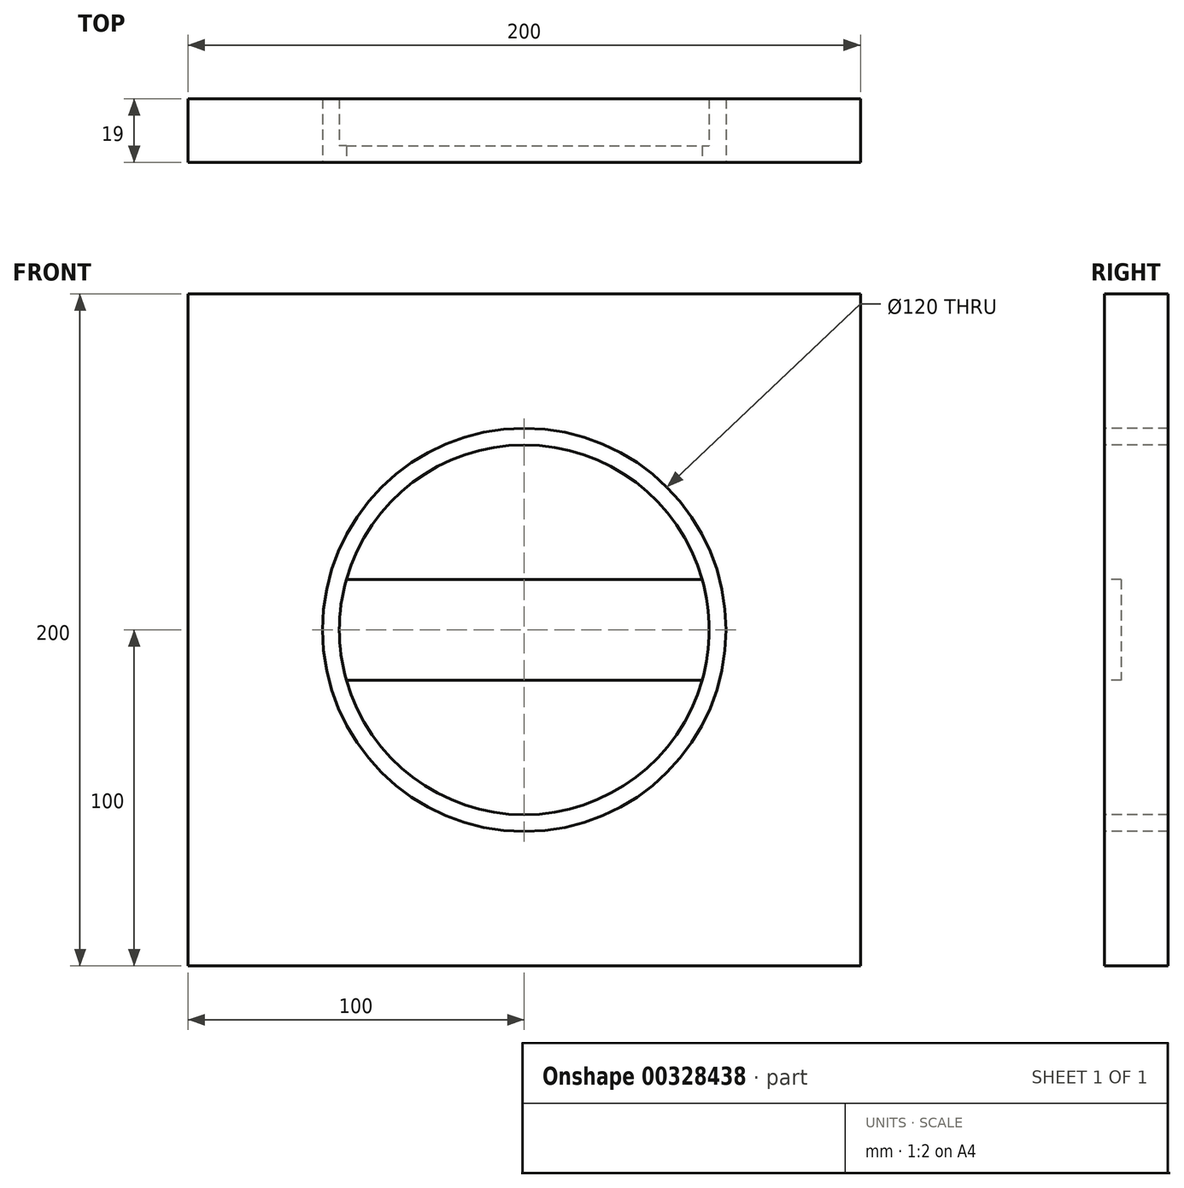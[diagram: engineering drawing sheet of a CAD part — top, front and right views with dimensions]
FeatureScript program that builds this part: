
annotation { "Feature Type Name" : "Feature", "Feature Type Description" : "" }
export const myFeature = defineFeature(function(context is Context, id is Id, definition is map)
    precondition{}
    {
        {
            var Q0;
            Q0=qCreatedBy(makeId("Front.planeOp"),FACE);
            var sketch = newSketch(context, id + "F0", { "sketchPlane" : qUnion([Q0])});
            skLineSegment(sketch, "E0.bottom", {"start": v(0, 0) * mm, "end": v(200, 0) * mm});
            skLineSegment(sketch, "E0.top", {"start": v(0, 200) * mm, "end": v(200, 200) * mm});
            skLineSegment(sketch, "E0.left", {"start": v(0, 0) * mm, "end": v(0, 200) * mm});
            skLineSegment(sketch, "E0.right", {"start": v(200, 0) * mm, "end": v(200, 200) * mm});
            skSolve(sketch);
        }
        {
            var Q0;
            Q0=makeQuery(id+"F0.imprint","IMPRINT",FACE,{"disambiguationData":[TD([[makeQuery(id+"F0.imprint","IMPRINT",EDGE,{"derivedFrom":sQuery(id+"F0.wireOp",EDGE,"E0.bottom")}),1.0]])]});
            extrude(context, id + "F1", {"entities" : qUnion([Q0]), "depth" : 19 * mm});
        }
        {
            var Q0;
            Q0=makeQuery(id+"F1.opExtrude","CAP_FACE",FACE,{"disambiguationData":[OSD([sQuery(id+"F0.wireOp",EDGE,"E0.bottom"),sQuery(id+"F0.wireOp",EDGE,"E0.top"),sQuery(id+"F0.wireOp",EDGE,"E0.left"),sQuery(id+"F0.wireOp",EDGE,"E0.right")])],"isStart":false});
            var sketch = newSketch(context, id + "F2", { "sketchPlane" : qUnion([Q0])});
            skArc(sketch, "E1", {"start": v(47.08, 115) * mm, "mid": v(45, 100) * mm, "end": v(47.08, 85) * mm});
            skLineSegment(sketch, "E2", {"start": v(47.08, 115) * mm, "end": v(152.92, 115) * mm});
            skLineSegment(sketch, "E3.MirrorCS", {"start": v(47.08, 85) * mm, "end": v(152.92, 85) * mm});
            skCircle(sketch, "E4.0", {"center": v(100, 100) * mm, "radius": 60 * mm});
            skArc(sketch, "E5.trimOffspring", {"start": v(152.92, 85) * mm, "mid": v(155, 100) * mm, "end": v(152.92, 115) * mm});
            skArc(sketch, "E6", {"start": v(47.08, 85) * mm, "mid": v(100, 45) * mm, "end": v(152.92, 85) * mm});
            skArc(sketch, "E7.trimOffspring", {"start": v(152.92, 115) * mm, "mid": v(100, 155) * mm, "end": v(47.08, 115) * mm});
            skSolve(sketch);
        }
        {
            var Q0;
            {var subQ0=sQuery(id+"F2.wireOp",EDGE,"E2");Q0=makeQuery(id+"F2.imprint","IMPRINT",FACE,{"disambiguationData":[TD([[makeQuery(id+"F2.imprint","IMPRINT",EDGE,{"derivedFrom":subQ0}),-1.0]])]});}
            extrude(context, id + "F3", {"entities" : qUnion([Q0]), "operationType" : NewBodyOperationType.REMOVE, "oppositeDirection" : true, "depth" : 5 * mm});
        }
        {
            var Q0;
            Q0=makeQuery(id+"F2.imprint","IMPRINT",FACE,{"disambiguationData":[TD([[makeQuery(id+"F2.imprint","IMPRINT",EDGE,{"derivedFrom":sQuery(id+"F2.wireOp",EDGE,"E1")}),-1.0]])]});
            extrude(context, id + "F4", {"entities" : qUnion([Q0]), "operationType" : NewBodyOperationType.REMOVE, "oppositeDirection" : true, "depth" : 19 * mm});
        }
    });
